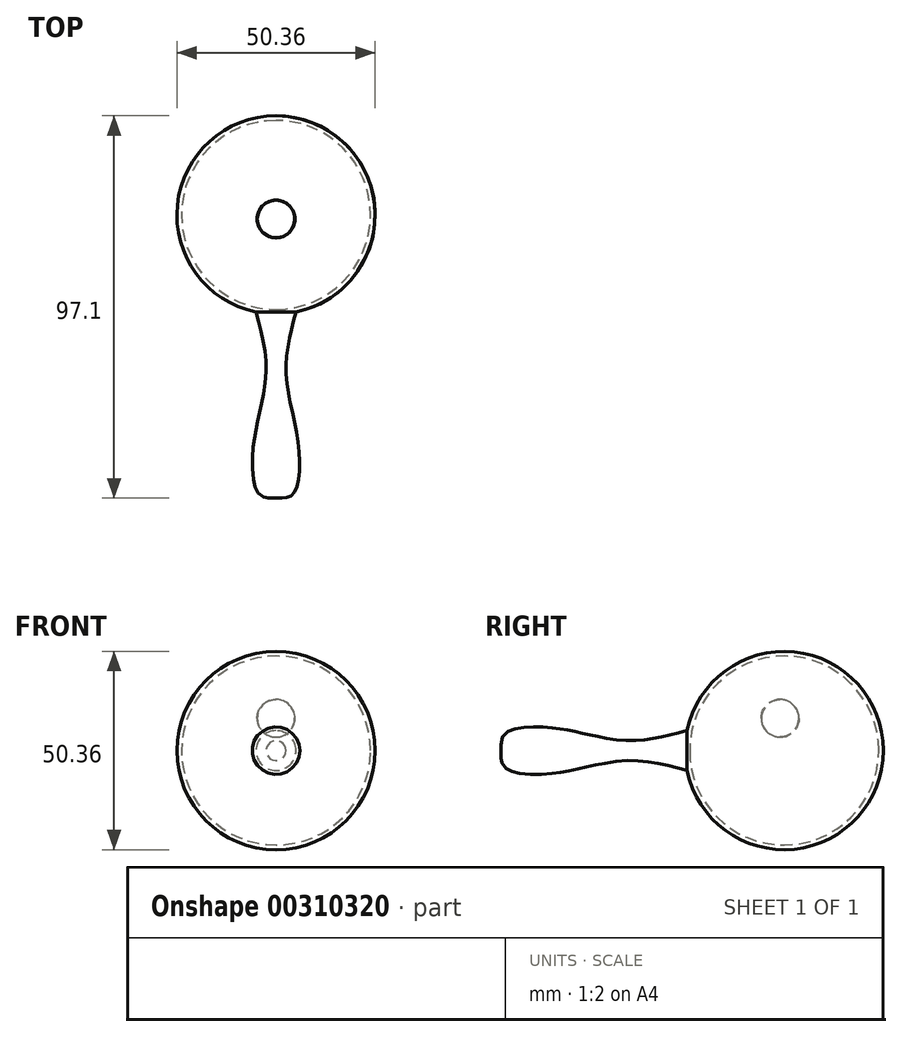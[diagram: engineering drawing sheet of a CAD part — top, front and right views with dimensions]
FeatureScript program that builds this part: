
annotation { "Feature Type Name" : "Feature", "Feature Type Description" : "" }
export const myFeature = defineFeature(function(context is Context, id is Id, definition is map)
    precondition{}
    {
        {
            var Q0;
            Q0=qCreatedBy(makeId("Top.planeOp"),FACE);
            var sketch = newSketch(context, id + "F0", { "sketchPlane" : qUnion([Q0])});
            skArc(sketch, "E0", {"start": v(5.07, 17.44) * mm, "mid": v(25.05, 44.66) * mm, "end": v(0, 67.3) * mm});
            skArc(sketch, "E1", {"start": v(0, 18.1) * mm, "mid": v(24, 42.11) * mm, "end": v(0, 66.11) * mm});
            skLineSegment(sketch, "E2", {"start": v(0, 67.3) * mm, "end": v(0, 66.11) * mm});
            skLineSegment(sketch, "E3", {"start": v(0, 18.1) * mm, "end": v(0, 16.93) * mm});
            skLineSegment(sketch, "E4", {"start": v(11.03, 19.47) * mm, "end": v(11.03, -33.35) * mm, "construction": true});
            skLineSegment(sketch, "E5", {"start": v(11.03, -33.35) * mm, "end": v(0, -33.35) * mm, "construction": true});
            skFitSpline(sketch, "E6", {"points": [v(5.07, 17.44) * mm, v(2.55, 1.95) * mm, v(5.75, -16.55) * mm, v(4.26, -28.89) * mm, v(0, -29.74) * mm], "startDerivative": vector(-14.42, -53.34) * mm, "endDerivative": vector(-31.91, 2.38) * mm});
            skLineSegment(sketch, "E7.trimOffspring", {"start": v(0, 18.1) * mm, "end": v(0, 16.93) * mm, "construction": true});
            skLineSegment(sketch, "E8", {"start": v(0, 67.3) * mm, "end": v(0, -29.74) * mm, "construction": true});
            skLineSegment(sketch, "E9", {"start": v(0, 18.1) * mm, "end": v(0, -29.74) * mm});
            skSolve(sketch);
        }
        {
            var Q0;
            Q0 = qSketchRegion(id + "F0", true);
            var Q1;
            Q1=sQuery(id+"F0.wireOp",EDGE,"E8");
            revolve(context, id + "F1", {"entities" : qUnion([Q0]), "axis" : qUnion([Q1]), "revolveType" : RevolveType.FULL});
        }
        {
            var Q0;
            Q0=qCreatedBy(makeId("Right.planeOp"),FACE);
            var sketch = newSketch(context, id + "F2", { "sketchPlane" : qUnion([Q0])});
            skArc(sketch, "E10", {"start": v(41.08, 3.43) * mm, "mid": v(45.84, 8.21) * mm, "end": v(41.08, 13) * mm});
            skLineSegment(sketch, "E11", {"start": v(41.08, 13) * mm, "end": v(41.08, 3.43) * mm});
            skSolve(sketch);
        }
        {
            var Q0;
            Q0=makeQuery(id+"F2.imprint","IMPRINT",FACE,{"disambiguationData":[TD([[makeQuery(id+"F2.imprint","IMPRINT",EDGE,{"derivedFrom":sQuery(id+"F2.wireOp",EDGE,"E10")}),1.0]])]});
            var Q1;
            Q1=sQuery(id+"F2.wireOp",EDGE,"E10");
            var Q2;
            Q2=sQuery(id+"F2.wireOp",EDGE,"E11");
            var Q3;
            Q3=sQuery(id+"F2.wireOp",EDGE,"E11");
            revolve(context, id + "F3", {"operationType" : NewBodyOperationType.ADD, "entities" : qUnion([Q0]), "surfaceEntities" : qUnion([Q1, Q2]), "axis" : qUnion([Q3]), "revolveType" : RevolveType.FULL});
        }
    });
